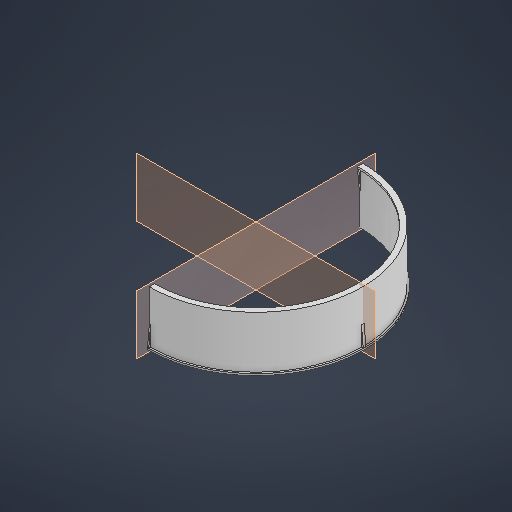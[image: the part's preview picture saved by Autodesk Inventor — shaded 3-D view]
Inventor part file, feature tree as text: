
AUTODESK INVENTOR PART (.ipt)
format: ipt  version: 2025 (Build 290162000, 162)  size: 519,168 bytes
history: native  units: in
note: dims shown in document units (in); Inventor stores cm internally (conversion verified against a paired STEP export)
features: rib x40, sketch x26, other x12, extrude x5, plane x1
ambient origin geometry x8: Origin, YZ Plane, XZ Plane, XY Plane, X Axis, Y Axis, Z Axis, Center Point
bodies: Solid1 (feature_tree)
feature tree (84):
  other  "Table"
  other  "C .Replace - 01"
  other  "C .Replace - 02"
  other  "C .Replace - 03"
  other  "C .Replace - 04"
  other  "C .Replace - 05"
  other  "C .Replace - 06"
  other  "C .Replace - 07"
  other  "C .Replace - 08"
  other  "C .Replace - 09"
  other  "C .Replace - 10"
  other  "C .Replace - Face"
  sketch  "Sketch1"  dims[d5=0.0in d7=0.0in]
  extrude  "Extrusion1"  TaperAngle=0.0deg  [1 undecoded]
  extrude  "Extrusion2"  Depth=10.0394in
  sketch  "Sketch2"  dims[d28=0.1969in d29=3.937in d31=360.0deg]
  extrude  "Extrusion7"  Depth=3.937in TaperAngle=360.0deg
  plane  "Work Plane2"
  extrude  "Extrusion8"  Depth=0.3937in
  extrude  "Extrusion30"  Depth=0.2165in
  sketch  "Sketch26"  dims[d236=0.3937in d237=0.0in]
  rib  "Rib2"
  rib  "Rib3"
  sketch  "Sketch27"  dims[d239=0.8661in]
  rib  "Rib4"
  rib  "Rib5"
  sketch  "Sketch28"  dims[d240=0.8661in]
  rib  "Rib6"
  rib  "Rib7"
  sketch  "Sketch29"  dims[d247=0.0984in]
  rib  "Rib8"
  rib  "Rib9"
  sketch  "Sketch30"  dims[d248=0.1181in d249=0.0in d250=0.0in d251=0.0394in d252=0.0394in]
  rib  "Rib10"
  rib  "Rib11"
  sketch  "Sketch31"  dims[d253=0.0984in]
  rib  "Rib12"
  rib  "Rib13"
  sketch  "Sketch32"  dims[d254=0.1181in d255=0.0in d256=0.0in d257=0.0394in d258=0.0394in]
  rib  "Rib14"
  rib  "Rib15"
  sketch  "Sketch33"  dims[d259=0.8661in]
  rib  "Rib16"
  rib  "Rib17"
  sketch  "Sketch34"  dims[d260=0.8661in]
  rib  "Rib18"
  rib  "Rib19"
  sketch  "Sketch35"  dims[d261=0.0984in]
  rib  "Rib20"
  rib  "Rib21"
  sketch  "Sketch36"  dims[d262=0.1181in d263=0.0in d264=0.0in d265=0.0394in d266=0.0394in]
  rib  "Rib22"
  rib  "Rib23"
  sketch  "Sketch37"  dims[d267=0.0984in]
  rib  "Rib24"
  rib  "Rib25"
  sketch  "Sketch38"  dims[d268=0.1181in d269=0.0in d270=0.0in d271=0.0394in d272=0.0394in]
  rib  "Rib26"
  rib  "Rib27"
  sketch  "Sketch39"  dims[d274=0.8661in]
  rib  "Rib28"
  rib  "Rib29"
  sketch  "Sketch40"  dims[d275=0.8661in]
  rib  "Rib30"
  rib  "Rib31"
  sketch  "Sketch41"  dims[d276=0.0984in]
  rib  "Rib32"
  rib  "Rib33"
  sketch  "Sketch42"  dims[d277=0.1181in d278=0.0in d279=0.0in d280=0.0394in d281=0.0394in]
  rib  "Rib34"
  rib  "Rib35"
  sketch  "Sketch43"  dims[d282=0.0984in]
  rib  "Rib36"
  rib  "Rib37"
  sketch  "Sketch44"  dims[d283=0.1181in d284=0.0in d285=0.0in d286=0.0394in d287=0.0394in]
  rib  "Rib38"
  rib  "Rib39"
  sketch  "Sketch45"  dims[d288=0.8661in d289=0.8661in d290=0.0984in d291=0.1181in d292=0.0in d293=0.0in d294=0.0394in d295=0.0394in d296=0.0984in d297=0.1181in d298=0.0in d299=0.0in d300=0.0394in d301=0.0394in d302=0.8661in d303=0.8661in d304=0.0984in d305=0.1181in d306=0.0in d307=0.0in d308=0.0394in d309=0.0394in d310=0.0984in d311=0.1181in d312=0.0in d313=0.0in d314=0.0394in d315=0.0394in d316=0.8661in d317=0.8661in d318=0.0984in d319=0.1181in d320=0.0in d321=0.0in d322=0.0394in d323=0.0394in d324=0.0984in d325=0.1181in d326=0.0in d327=0.0in d328=0.0394in d329=0.0394in d330=0.8661in d331=0.8661in d332=0.0984in d333=0.1181in d334=0.0in d335=0.0in d336=0.0394in d337=0.0394in d338=0.0984in d339=0.1181in d340=0.0in d341=0.0in d342=0.0394in d343=0.0394in d344=0.8661in d345=0.8661in d346=0.0984in d347=0.1181in d348=0.0in d349=0.0in d350=0.0394in d351=0.0394in d352=0.0984in d353=0.1181in d354=0.0in d355=0.0in d356=0.0394in d357=0.0394in d358=0.8661in d359=0.8661in d360=0.0984in d361=0.1181in d362=0.0in d363=0.0in d364=0.0394in d365=0.0394in d366=0.0984in d367=0.1181in d368=0.0in d369=0.0in d370=0.0394in d371=0.0394in d372=0.8661in d373=0.8661in d374=0.0984in d375=0.1181in d376=0.0in d377=0.0in d378=0.0394in d379=0.0394in d380=0.0984in d381=0.1181in d382=0.0in d383=0.0in d384=0.0394in d385=0.0394in d386=0.8661in d387=0.8661in d388=0.0984in d389=0.1181in d390=0.0in d391=0.0in d392=0.0394in d393=0.0394in d394=0.0984in d395=0.1181in d396=0.0in d397=0.0in d398=0.0394in d399=0.0394in d401=0.8661in d402=0.0984in d403=0.1181in d404=0.0in d405=0.0in d406=0.0394in d407=0.0394in d408=0.0984in d409=0.1181in d410=0.0in d411=0.0in d412=0.0394in d413=0.0394in d414=0.8661in d415=0.8661in d416=0.0984in d417=0.1181in d418=0.0in d419=0.0in d420=0.0394in d421=0.0394in d422=0.0984in d423=0.1181in d424=0.0in d425=0.0in d426=0.0394in d427=0.0394in d428=0.8661in d429=0.8661in d430=0.0984in d431=0.1181in d432=0.0in d433=0.0in d434=0.0394in d435=0.0394in d436=0.0984in d437=0.1181in d438=0.0in d439=0.0in d440=0.0394in d441=0.0394in d442=0.8661in d443=0.8661in d444=0.0984in d445=0.1181in d446=0.0in d447=0.0in d448=0.0394in d449=0.0394in d450=0.0984in d451=0.1181in d452=0.0in d453=0.0in d454=0.0394in d455=0.0394in d456=0.8661in d457=0.8661in d458=0.0984in d459=0.1181in d460=0.0in d461=0.0in d462=0.0394in d463=0.0394in d464=0.0984in d465=0.1181in d466=0.0in d467=0.0in d468=0.0394in d469=0.0394in d470=0.8661in d471=0.8661in d472=0.0984in d473=0.1181in d474=0.0in d475=0.0in d476=0.0394in d477=0.0394in d478=0.0984in d479=0.1181in d480=0.0in d481=0.0in d482=0.0394in d483=0.0394in d484=0.8661in d485=0.8661in d486=0.0984in d487=0.1181in d488=0.0in d489=0.0in d490=0.0394in d491=0.0394in d492=0.0984in d493=0.1181in d494=0.0in d495=0.0in d496=0.0394in d497=0.0394in d498=0.8661in d499=0.8661in d500=0.0984in d501=0.1181in d502=0.0in d503=0.0in d504=0.0394in d505=0.0394in d506=0.0984in d507=0.1181in d508=0.0in d509=0.0in d510=0.0394in d511=0.0394in d512=0.8661in d513=0.8661in d514=0.0984in d515=0.1181in d516=0.0in d517=0.0in d518=0.0394in d519=0.0394in d520=0.0984in d521=0.1181in d522=0.0in d523=0.0in d524=0.0394in d525=0.0394in d113=0.0197in d114=0.0344in d115=0.0197in d116=0.0344in d167=0.0197in d168=0.0344in d169=0.0197in d170=0.0344in d215=0.0197in d216=0.0344in d217=0.0197in d218=0.0344in d219=0.0in d220=0.0in]
  rib  "Rib40"
  rib  "Rib41"
  sketch  "Sketch3"  dims[d33=0.3937in d34=0.0in d52=4.5276in]
  sketch  "Sketch Circular Pattern1"  dims[d18=0.0in d27=10.0394in]
  sketch  "Sketch24"  dims[d232=2.3622in d234=360.0deg]
  sketch  "Sketch Circular Pattern4"  dims[d230=4.0157in d231=0.2165in]
note: 1 required parameter value undecoded (feature->parameter linkage not recoverable at this tier; creation-order binding heuristic only, values carry confidence <= 0.55)
